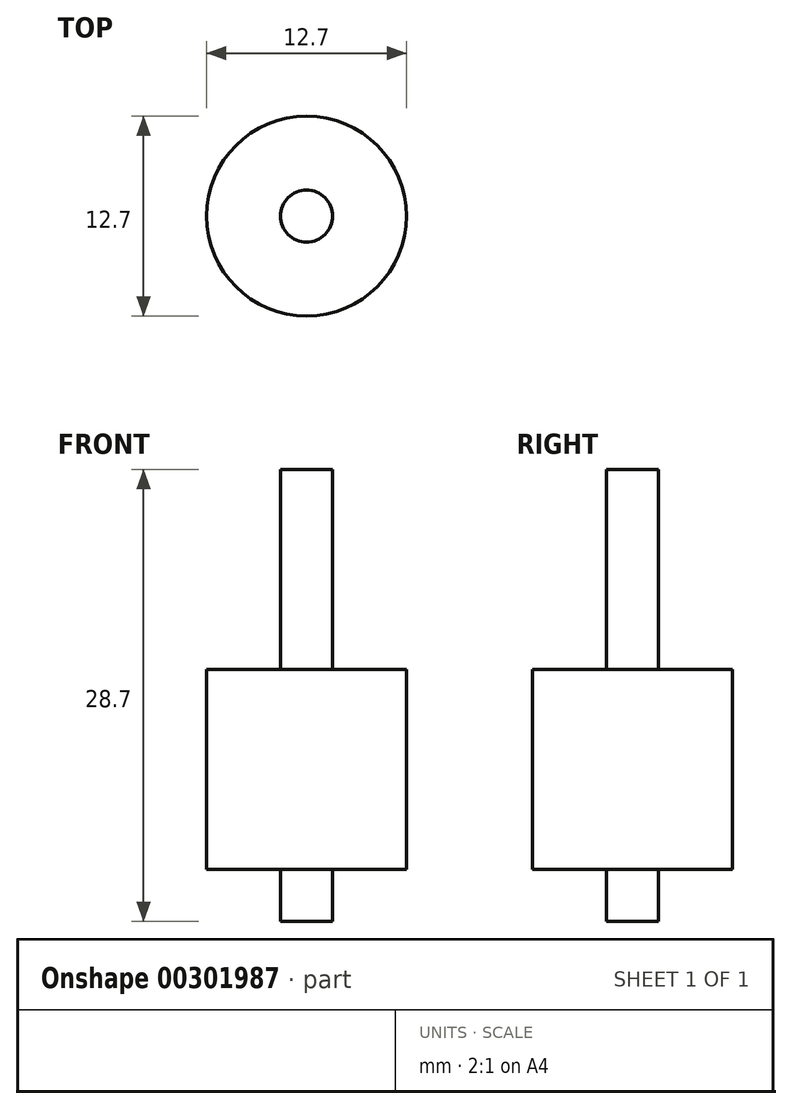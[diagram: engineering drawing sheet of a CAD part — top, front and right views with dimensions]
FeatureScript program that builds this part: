
annotation { "Feature Type Name" : "Feature", "Feature Type Description" : "" }
export const myFeature = defineFeature(function(context is Context, id is Id, definition is map)
    precondition{}
    {
        {
            var Q0;
            Q0=qCreatedBy(makeId("Top.planeOp"),FACE);
            var sketch = newSketch(context, id + "F0", { "sketchPlane" : qUnion([Q0])});
            skCircle(sketch, "E0", {"center": v(-24.94, 17.33) * mm, "radius": 6.35 * mm});
            skSolve(sketch);
        }
        {
            var Q0;
            Q0=makeQuery(id+"F0.imprint","IMPRINT",FACE,{"disambiguationData":[TD([[makeQuery(id+"F0.imprint","IMPRINT",EDGE,{"derivedFrom":sQuery(id+"F0.wireOp",EDGE,"E0")}),1.0]])]});
            extrude(context, id + "F1", {"entities" : qUnion([Q0]), "oppositeDirection" : true, "depth" : 12.7 * mm, "offsetDistance" : 25.4 * mm});
        }
        {
            var Q0;
            Q0=qCreatedBy(makeId("Top.planeOp"),FACE);
            var sketch = newSketch(context, id + "F2", { "sketchPlane" : qUnion([Q0])});
            skCircle(sketch, "E1", {"center": v(-24.94, 17.33) * mm, "radius": 1.65 * mm});
            skSolve(sketch);
        }
        {
            var Q0;
            Q0=makeQuery(id+"F2.imprint","IMPRINT",FACE,{"disambiguationData":[TD([[makeQuery(id+"F2.imprint","IMPRINT",EDGE,{"derivedFrom":sQuery(id+"F2.wireOp",EDGE,"E1")}),1.0]])]});
            extrude(context, id + "F3", {"entities" : qUnion([Q0]), "operationType" : NewBodyOperationType.ADD, "depth" : 12.7 * mm, "offsetDistance" : 25.4 * mm});
        }
        {
            var Q0;
            Q0=makeQuery(id+"F1.opExtrude","CAP_FACE",FACE,{"disambiguationData":[OSD([sQuery(id+"F0.wireOp",EDGE,"E0")])],"isStart":false});
            var sketch = newSketch(context, id + "F4", { "sketchPlane" : qUnion([Q0])});
            skCircle(sketch, "E2", {"center": v(-24.94, -17.33) * mm, "radius": 1.65 * mm});
            skSolve(sketch);
        }
        {
            var Q0;
            Q0=makeQuery(id+"F4.imprint","IMPRINT",FACE,{"disambiguationData":[TD([[makeQuery(id+"F4.imprint","IMPRINT",EDGE,{"derivedFrom":sQuery(id+"F4.wireOp",EDGE,"E2")}),1.0]])]});
            extrude(context, id + "F5", {"entities" : qUnion([Q0]), "operationType" : NewBodyOperationType.ADD, "depth" : 3.3 * mm, "offsetDistance" : 25.4 * mm});
        }
    });
